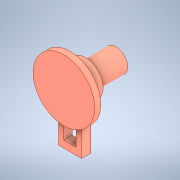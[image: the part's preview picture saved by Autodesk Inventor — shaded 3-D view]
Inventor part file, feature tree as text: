
AUTODESK INVENTOR PART (.ipt)
format: ipt  version: 2020.1 (Build 241239000, 239)  size: 248,832 bytes
history: native  units: in
note: dims shown in document units (in); Inventor stores cm internally (conversion verified against a paired STEP export)
features: extrude x5, sketch x5, projected_geometry x3, other x1, plane x1, fillet x1
ambient origin geometry x8: Origin, YZ Plane, XZ Plane, XY Plane, X Axis, Y Axis, Z Axis, Center Point
bodies: Solid1 (feature_tree)
feature tree (16):
  parser-record x1  (decoder bookkeeping rows leaked as tree rows — omitted from the tree; the rows remain in map.json)
  extrude  "Extrusion1"  Depth=0.0787in
  extrude  "Extrusion2"  Depth=0.2953in
  plane  "Work Plane2"
  extrude  "Extrusion7"  TaperAngle=0.0deg  [1 undecoded]
  extrude  "Extrusion8"  Depth=0.0787in
  extrude  "Extrusion9"  TaperAngle=0.0deg  [1 undecoded]
  fillet  "Fillet2"  Radius=0.7218in
  sketch  "Sketch1"  dims[d0=0.7874in d1=0.0787in]
  sketch  "Sketch2"  dims[d2=0.0in d3=0.2953in]
  sketch  "Sketch7"  dims[d4=0.5906in d5=0.0in]
  projected_geometry  "Projected Loop3"
  sketch  "Sketch8"  dims[d26=-0.3937in d27=0.0787in]
  projected_geometry  "Projected Loop4"
  sketch  "Sketch9"  dims[d28=0.0787in d29=0.0in d31=0.7218in d32=0.1181in d33=0.0in d34=0.0787in d35=0.1575in d36=0.315in d37=0.315in d38=0.3937in d39=0.0137in d40=0.0098in d41=0.0344in]
  projected_geometry  "Projected Loop5"
note: 2 required parameter values undecoded (feature->parameter linkage not recoverable at this tier; creation-order binding heuristic only, values carry confidence <= 0.55)
note: 1 file-system path scrubbed to <path> (originals preserved in map.json)
